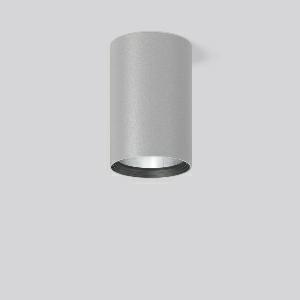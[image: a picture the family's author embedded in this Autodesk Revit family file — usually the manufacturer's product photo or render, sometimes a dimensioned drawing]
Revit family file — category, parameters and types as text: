
# Revit family: heledon_maxi_a_931218_004_3_50d6
name_source: partatom
category: Lighting Fixtures
units: mm (PartAtom-declared; Revit-internal decimal feet)

## family parameters
Cut with Voids When Loaded = No
Host = Face
Light Source = No
Part Type = Normal
Room Calculation Point = No
Round Connector Dimension = Use Diameter
Shared = No

## types (1)
- HELEDON maxi A (1 x LED Modul 935, 3400 lm, 3500)
    Apparent Load = 25 VA
    Approval mark = CE
    CIE Flux Codes = 100 100 100 100 100
    Color Rendering = 92
    Color Temperature = 3500
    Default Elevation = 1800 mm
    Description = Series: HELEDON maxi
Cylindrical surface-mounted downlight. Housing: die-cast aluminium, powder-coated. Internal ceiling frame polycarbonate with bayonet mounting. Black plastic ring and recessed LED to prevent glare from the side. Optical assembly with reflector made of MIRO-Silver with 98% total light reflection for outstanding efficiency - can be changed without tools. Best colour rendering index Ra>90. Suitable for Ceiling mounting. Easy installation with a separate ceiling frame with bayonet mounting and plug connection. Driver integrated. Connected via plug-in connector. High quality converter without flickering and stroboscopic effect. The following accessories can be mounted without use of tools: interchangeable lenses, decorative glasses, honeycomb louvre, clear and frosted diffusers, white interchangeable plastic ring. 
Colour: silver
Diameter: 123 mm
Height: 183 mm
Lamp: LED
Socket: without socket
Colour temperature: 3500K
Colour rendering index (CRI): 92
System power: 25 W
Rated luminous flux: 3400 lm
Luminous efficiency: 136 lm/W
Control gear: Regulated power supply
Protection class: I
Type of protection: IP 20
    Height = 183 mm
    Lamp = 1 x LED Modul 935
    Lamp Light Flux = 3400 lm
    Lamp count = 1
    Length = 123 mm
    Lifetime = 50000 h
    Luminous efficacy = 136 lm/W
    Manufacturer = RZB
    ModVariant = No
    Model = 931218.004.3
    Mounting Place = Ceiling
    Mounting Type = Surface mounted
    Number of Poles = 1
    OnlyDefault = Yes
    Power Factor = 1
    Product Name = HELEDON maxi A
    Product group = Surface mounted downlights
    ProductGroupID = 302
    Protection Class = Protection class I
    Protection Degree = IP 20
    RLX_Detail_Level = 1
    RLX_Emergency_Light_Flux = 0 lm
    RLX_Emergency_Type = 0
    RLX_Emergency_Type_DB = No
    RlxData = <blob elided: 99053 chars, md5=3f59c6a0>
    Socket = socket
    Standby Power = 0 W
    System Light Flux = 3400 lm
    System Power = 25 W
    Type Comments = Product without accessories
    Type Image = 931192.004.jpg
    URL = http://relux.com
    VarID = ---
    Voltage = 230 V
    Voltage Range = 220-240 V
    Weight = 0.00 kg
    Width = 0 mm  [stored 0 ft]

note: [stored X ft] marks values corroborated as IEEE doubles in the binary element streams (Revit-internal decimal feet)

## geometry (parser evidence)
native form markers: Blend x4, Sweep x10
no freeform markers — native parametric forms only
